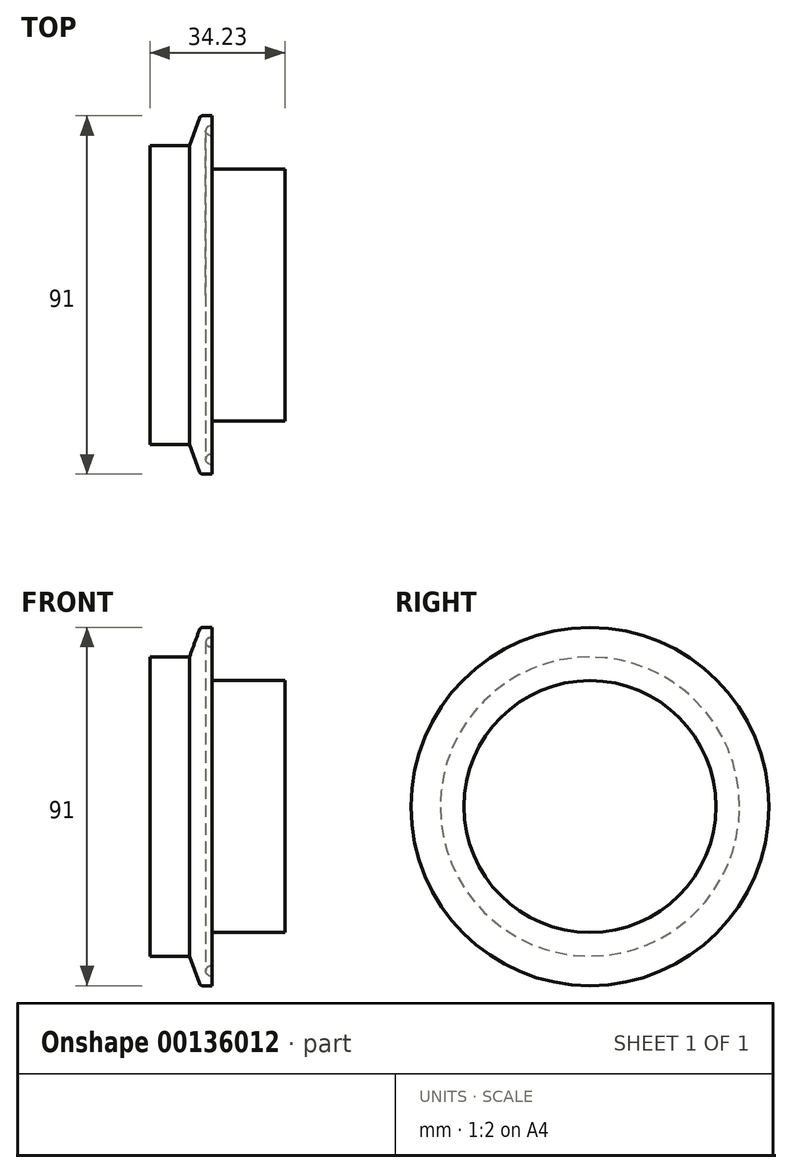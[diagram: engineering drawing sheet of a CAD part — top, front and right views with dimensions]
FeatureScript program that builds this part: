
annotation { "Feature Type Name" : "Feature", "Feature Type Description" : "" }
export const myFeature = defineFeature(function(context is Context, id is Id, definition is map)
    precondition{}
    {
        {
            var Q0;
            Q0=qCreatedBy(makeId("Top.planeOp"),FACE);
            var sketch = newSketch(context, id + "F0", { "sketchPlane" : qUnion([Q0])});
            skLineSegment(sketch, "E0", {"start": v(-75.9, 0) * mm, "end": v(75.2, 0) * mm, "construction": true});
            skSolve(sketch);
        }
        {
            var Q0;
            Q0=qCreatedBy(makeId("Front.planeOp"),FACE);
            var sketch = newSketch(context, id + "F1", { "sketchPlane" : qUnion([Q0])});
            skLineSegment(sketch, "E1", {"start": v(0, 45.5) * mm, "end": v(0, 43.75) * mm});
            skLineSegment(sketch, "E2", {"start": v(0, 45.5) * mm, "end": v(-2.44, 45.5) * mm});
            skLineSegment(sketch, "E3", {"start": v(-3.2, 44.97) * mm, "end": v(-5.73, 38) * mm});
            skLineSegment(sketch, "E4", {"start": v(-5.73, 38) * mm, "end": v(-15.73, 38) * mm});
            skLineSegment(sketch, "E5", {"start": v(0, 32) * mm, "end": v(23.5, 32) * mm});
            skLineSegment(sketch, "E6", {"start": v(23.5, 32) * mm, "end": v(23.5, 0) * mm});
            skLineSegment(sketch, "E7", {"start": v(23.5, 0) * mm, "end": v(-15.73, 0) * mm});
            skLineSegment(sketch, "E8", {"start": v(-15.73, 0) * mm, "end": v(-15.73, 38) * mm});
            skLineSegment(sketch, "E9", {"start": v(0, 0) * mm, "end": v(0, 32) * mm, "construction": true});
            skPoint(sketch, "E10.visualSharp", {"position": v(-3, 45.5) * mm});
            skArc(sketch, "E10.filletArc", {"start": v(-2.44, 45.5) * mm, "mid": v(-2.9, 45.36) * mm, "end": v(-3.2, 44.97) * mm});
            skArc(sketch, "E11", {"start": v(-0.87, 42.85) * mm, "mid": v(-1.6, 41.75) * mm, "end": v(-0.87, 40.65) * mm});
            skLineSegment(sketch, "E12", {"start": v(-0.87, 42.85) * mm, "end": v(-0.49, 43.02) * mm});
            skLineSegment(sketch, "E13", {"start": v(-0.87, 40.65) * mm, "end": v(-0.49, 40.48) * mm});
            skLineSegment(sketch, "E14", {"start": v(-0.4, 41.75) * mm, "end": v(1.9, 41.75) * mm, "construction": true});
            skLineSegment(sketch, "E15.trimOffspring", {"start": v(0, 39.75) * mm, "end": v(0, 32) * mm});
            skArc(sketch, "E16.filletArc", {"start": v(-0.49, 43.02) * mm, "mid": v(-0.13, 43.31) * mm, "end": v(0, 43.75) * mm});
            skPoint(sketch, "E17.visualSharp", {"position": v(0, 40.28) * mm});
            skArc(sketch, "E17.filletArc", {"start": v(0, 39.75) * mm, "mid": v(-0.13, 40.19) * mm, "end": v(-0.49, 40.48) * mm});
            skSolve(sketch);
        }
        {
            var Q0;
            Q0 = qSketchRegion(id + "F1", true);
            var Q1;
            Q1=sQuery(id+"F0.wireOp",EDGE,"E0");
            revolve(context, id + "F2", {"entities" : qUnion([Q0]), "axis" : qUnion([Q1]), "revolveType" : RevolveType.FULL});
        }
        {
            var Q0;
            Q0=makeQuery(id+"F2.opRevolve","SWEPT_FACE",FACE,{"disambiguationData":[OSD([sQuery(id+"F1.wireOp",EDGE,"E6")])]});
            var sketch = newSketch(context, id + "F3", { "sketchPlane" : qUnion([Q0])});
            skCircle(sketch, "E18.0", {"center": v(0, 0) * mm, "radius": 32 * mm});
            skSolve(sketch);
        }
        {
            var Q0;
            Q0 = qSketchRegion(id + "F3", true);
            extrude(context, id + "F4", {"entities" : qUnion([Q0]), "operationType" : NewBodyOperationType.REMOVE, "oppositeDirection" : true, "depth" : 5 * mm});
        }
    });
